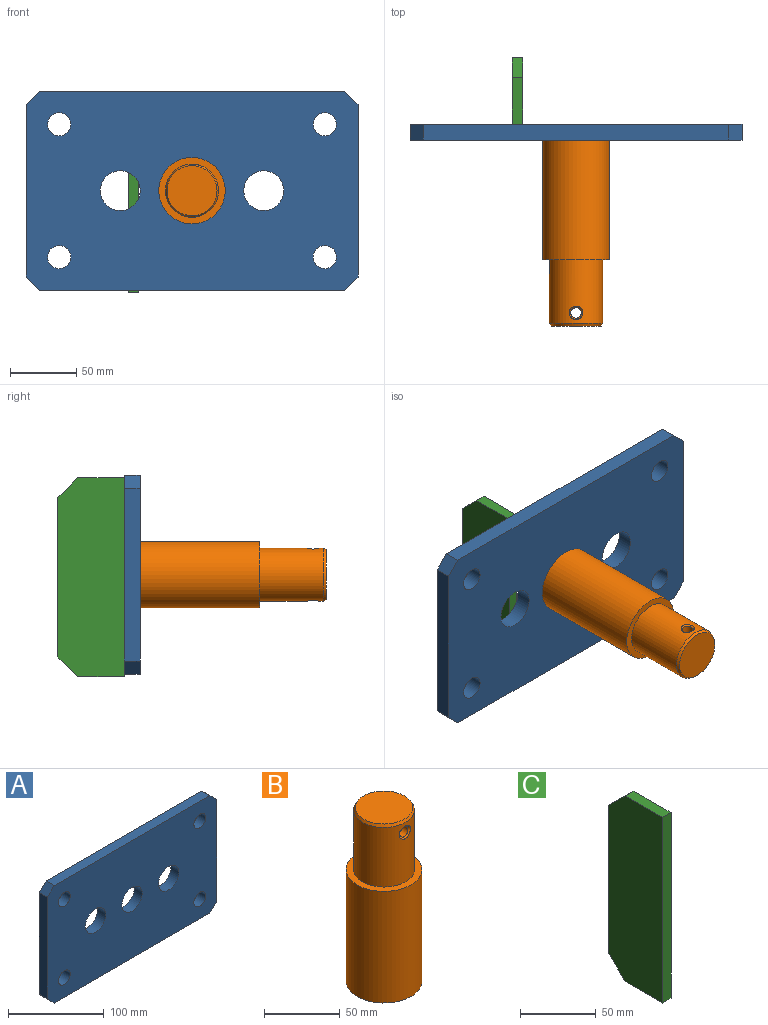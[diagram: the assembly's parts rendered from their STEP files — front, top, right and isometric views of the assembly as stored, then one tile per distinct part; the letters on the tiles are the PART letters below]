
ASSEMBLY  parts=3 mates=2
PART A: 17 faces, bbox 250x12x150 mm
  f0: plane 230x12mm, normal (0,0,-1), area 2760mm2, adj f4,f5,f6,f9
  f1: plane 130x12mm, normal (1,0,0), area 1560mm2, adj f4,f5,f7,f9
  f2: plane 230x12mm, normal (0,0,1), area 2760mm2, adj f4,f5,f7,f8
  f3: plane 130x12mm, normal (-1,0,0), area 1560mm2, adj f4,f5,f6,f8
  f4: plane 250x150mm, normal (0,-1,0), area 34217.3mm2, adj f0,f1,f2,f3,f6,f7,f8,f9
  f5: plane 250x150mm, normal (0,1,0), area 34217.3mm2, adj f0,f1,f2,f3,f6,f7,f8,f9
  f6: plane 12x10mm, normal (-0.71,0,-0.71), area 169.7mm2, adj f0,f3,f4,f5
  f7: plane 12x10mm, normal (0.71,0,0.71), area 169.7mm2, adj f1,f2,f4,f5
  f8: plane 12x10mm, normal (-0.71,0,0.71), area 169.7mm2, adj f2,f3,f4,f5
  f9: plane 12x10mm, normal (0.71,0,-0.71), area 169.7mm2, adj f0,f1,f4,f5
  f10: cylinder r=8.75mm len=17.5mm, axis (0,-1,0), area 659.7mm2, adj f4,f5
  f11: cylinder r=8.75mm len=17.5mm, axis (0,-1,0), area 659.7mm2, adj f4,f5
  f12: cylinder r=8.75mm len=17.5mm, axis (0,-1,0), area 659.7mm2, adj f4,f5
  f13: cylinder r=8.75mm len=17.5mm, axis (0,-1,0), area 659.7mm2, adj f4,f5
  f14: cylinder r=15mm len=30mm, axis (0,-1,0), area 1131mm2, adj f4,f5
  f15: cylinder r=15mm len=30mm, axis (0,-1,0), area 1131mm2, adj f4,f5
  f16: cylinder r=15mm len=30mm, axis (0,-1,0), area 1131mm2, adj f4,f5
PART B: 12 faces, bbox 50x50x150 mm
  f0: cylinder r=20mm len=48mm, axis (0,0,1), area 5865.1mm2, adj f6,f9,f10,f11
  f1: cylinder r=25mm len=90mm, axis (0,0,-1), area 14137.2mm2, adj f2,f6
  f2: plane 50x50mm, normal (0,0,-1), area 1266mm2, adj f1,f3
  f3: cylinder r=14.9mm len=29.8mm, axis (0,0,1), area 468.1mm2, adj f2,f5
  f4: plane 19.8x19.8mm, normal (0,0,-1), area 307.9mm2, adj f5
  f5: cone r=14.9mm half-angle=45deg, axis (0,0,1), area 550.9mm2, adj f3,f4
  f6: plane 50x50mm, normal (0,0,1), area 706.9mm2, adj f0,f1
  f7: plane 37.69x37.69mm, normal (0,0,1), area 1115.7mm2, adj f9
  f8: cylinder r=4mm len=38mm, axis (0,-1,0), area 955mm2, adj f10,f11
  f9: cone r=18.85mm half-angle=30deg, axis (0,0,-1), area 281.8mm2, adj f0,f7
  f10: bspline ~10.53x10mm, area 43.3mm2, adj f0,f8
  f11: bspline ~10.53x10mm, area 43.3mm2, adj f0,f8
PART C: 8 faces, bbox 8x50x150 mm
  f0: plane 150x50mm, normal (-1,0,0), area 7275mm2, adj f1,f3,f4,f5,f6,f7
  f1: plane 35x8mm, normal (0,0,1), area 280mm2, adj f0,f2,f5,f6
  f2: plane 150x50mm, normal (1,0,0), area 7275mm2, adj f1,f3,f4,f5,f6,f7
  f3: plane 35x8mm, normal (0,0,-1), area 280mm2, adj f0,f2,f5,f7
  f4: plane 120x8mm, normal (0,1,0), area 960mm2, adj f0,f2,f6,f7
  f5: plane 150x8mm, normal (0,-1,0), area 1200mm2, adj f0,f1,f2,f3
  f6: plane 15x15mm, normal (0,0.71,0.71), area 169.7mm2, adj f0,f1,f2,f4
  f7: plane 15x15mm, normal (0,0.71,-0.71), area 169.7mm2, adj f0,f2,f3,f4
PLACE A at identity fixed
PLACE B rot(axis=(1,0,0),90deg) t=(0,4,0)mm
PLACE C t=(10.08,0,-1.98)mm
MATE planar C.f5 <-> A.f15  axis (0,-1,0) through (-43.92,6,-1.98)mm
MATE fastened B.f0 <-> A.f14  axis (0,1,0) through (0,-6,0)mm
